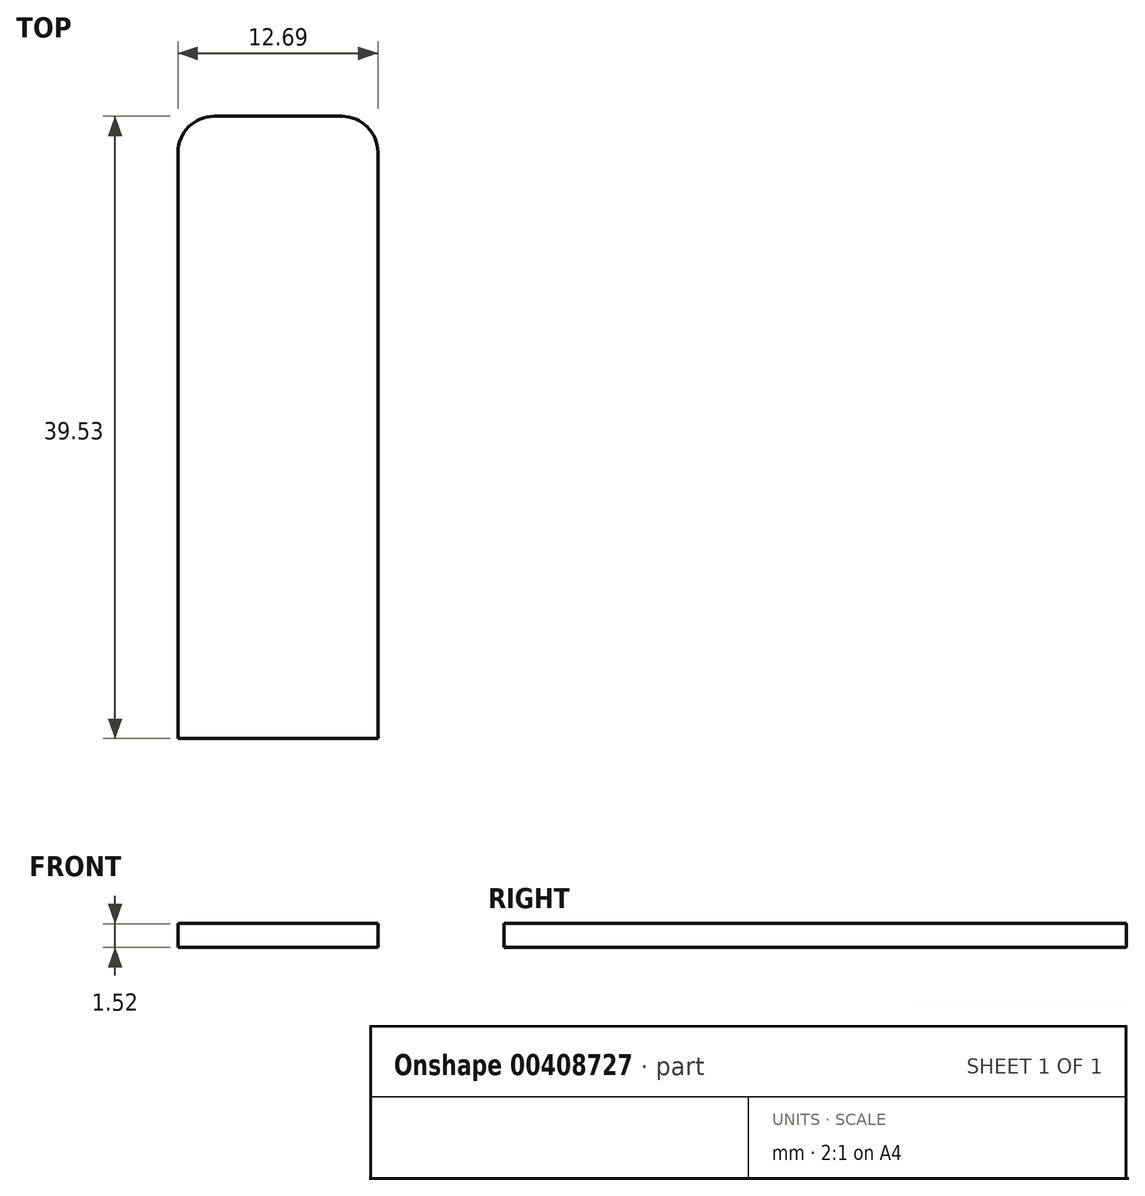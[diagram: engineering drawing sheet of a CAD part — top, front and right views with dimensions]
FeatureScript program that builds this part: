
annotation { "Feature Type Name" : "Feature", "Feature Type Description" : "" }
export const myFeature = defineFeature(function(context is Context, id is Id, definition is map)
    precondition{}
    {
        {
            var Q0;
            Q0=qCreatedBy(makeId("Top.planeOp"),FACE);
            var sketch = newSketch(context, id + "F0", { "sketchPlane" : qUnion([Q0])});
            skLineSegment(sketch, "E0.bottom", {"start": v(-17.34, -15.67) * mm, "end": v(-4.65, -15.67) * mm});
            skLineSegment(sketch, "E0.top", {"start": v(-17.34, 23.86) * mm, "end": v(-4.65, 23.86) * mm});
            skLineSegment(sketch, "E0.left", {"start": v(-17.34, -15.67) * mm, "end": v(-17.34, 23.86) * mm});
            skLineSegment(sketch, "E0.right", {"start": v(-4.65, -15.67) * mm, "end": v(-4.65, 23.86) * mm});
            skLineSegment(sketch, "E1.bottom", {"start": v(-15.36, -15.67) * mm, "end": v(-6.55, -15.67) * mm});
            skLineSegment(sketch, "E2.bottom", {"start": v(-15.01, -15.67) * mm, "end": v(-7.5, -15.67) * mm});
            skLineSegment(sketch, "E2.top", {"start": v(-15.01, -19.74) * mm, "end": v(-7.5, -19.74) * mm});
            skLineSegment(sketch, "E2.left", {"start": v(-15.01, -15.67) * mm, "end": v(-15.01, -19.74) * mm});
            skLineSegment(sketch, "E2.right", {"start": v(-7.5, -15.67) * mm, "end": v(-7.5, -19.74) * mm});
            skSolve(sketch);
        }
        {
            var Q0;
            Q0=makeQuery(id+"F0.imprint","IMPRINT",FACE,{"disambiguationData":[TD([[makeQuery(id+"F0.imprint","IMPRINT",EDGE,{"derivedFrom":sQuery(id+"F0.wireOp",EDGE,"E0.top")}),-1.0]])]});
            var Q1;
            Q1=makeQuery(id+"F0.imprint","IMPRINT",FACE,{"disambiguationData":[TD([[makeQuery(id+"F0.imprint","IMPRINT",EDGE,{"derivedFrom":sQuery(id+"F0.wireOp",EDGE,"E1.bottom")}),-1.0]])]});
            var Q2;
            Q2=makeQuery(id+"F0.imprint","IMPRINT",FACE,{"disambiguationData":[TD([[makeQuery(id+"F0.imprint","IMPRINT",EDGE,{"derivedFrom":sQuery(id+"F0.wireOp",EDGE,"E2.bottom")}),-1.0]])]});
            extrude(context, id + "F1", {"entities" : qUnion([Q0, Q1, Q2]), "depth" : 1.52 * mm});
        }
        {
            var Q0;
            Q0=makeQuery(id+"F1.opExtrude","SWEPT_EDGE",EDGE,{"disambiguationData":[OSD([sQuery(id+"F0.wireOp",EDGE,"E0.top"),sQuery(id+"F0.wireOp",EDGE,"E0.right")])]});
            var Q1;
            Q1=makeQuery(id+"F1.opExtrude","SWEPT_EDGE",EDGE,{"disambiguationData":[OSD([sQuery(id+"F0.wireOp",EDGE,"E0.top"),sQuery(id+"F0.wireOp",EDGE,"E0.left")])]});
            fillet(context, id + "F2", {"entities" : qUnion([Q0, Q1]), "radius" : 2.3 * mm, "tangentPropagation" : true, "allowEdgeOverflow" : false});
        }
    });
